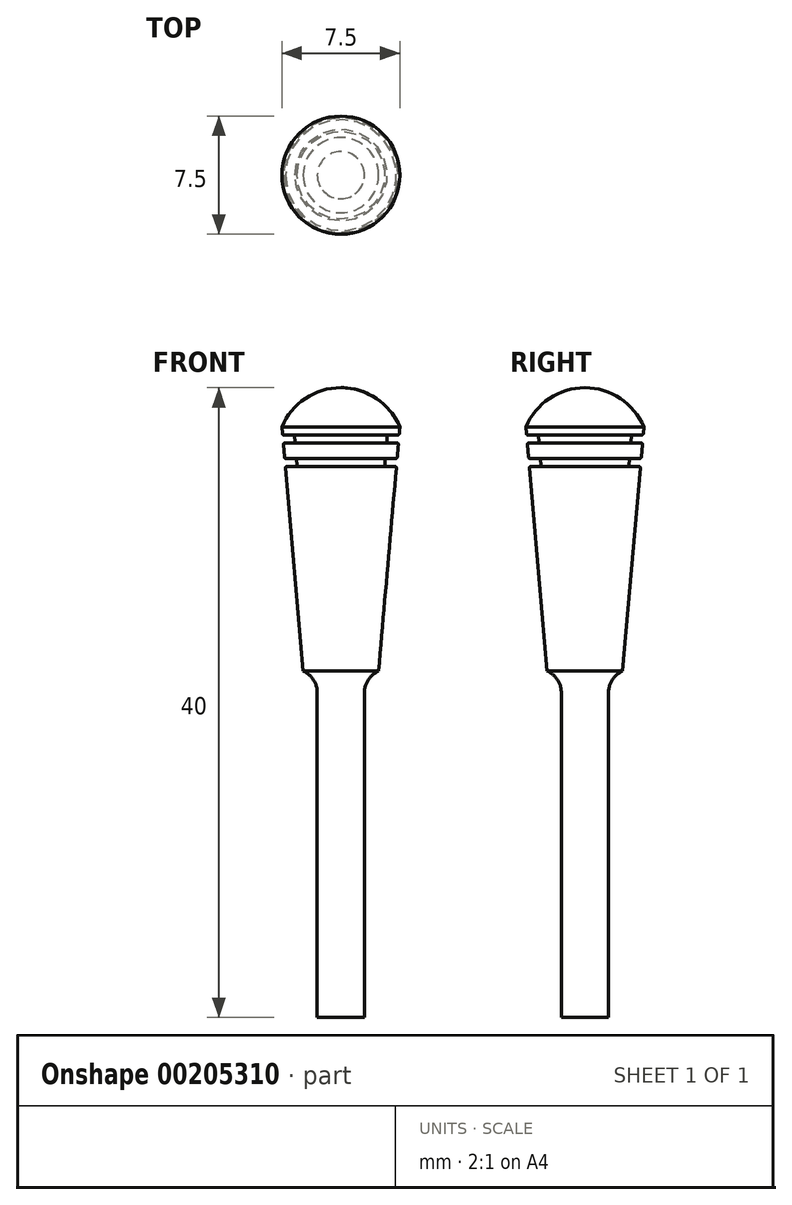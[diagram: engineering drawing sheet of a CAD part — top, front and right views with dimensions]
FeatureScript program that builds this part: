
annotation { "Feature Type Name" : "Feature", "Feature Type Description" : "" }
export const myFeature = defineFeature(function(context is Context, id is Id, definition is map)
    precondition{}
    {
        {
            var Q0;
            Q0=qCreatedBy(makeId("Front.planeOp"),FACE);
            var sketch = newSketch(context, id + "F0", { "sketchPlane" : qUnion([Q0])});
            skLineSegment(sketch, "E0.bottom", {"start": v(0, 0) * mm, "end": v(1.5, 0) * mm});
            skLineSegment(sketch, "E0.left", {"start": v(0, 0) * mm, "end": v(0, 21.67) * mm});
            skLineSegment(sketch, "E0.right", {"start": v(1.5, 0) * mm, "end": v(1.5, 22) * mm});
            skLineSegment(sketch, "E1", {"start": v(1.5, 22) * mm, "end": v(2.4, 22) * mm});
            skLineSegment(sketch, "E2", {"start": v(2.4, 22) * mm, "end": v(3.53, 35) * mm});
            skLineSegment(sketch, "E3", {"start": v(0, 21.67) * mm, "end": v(0, 37.5) * mm});
            skLineSegment(sketch, "E4", {"start": v(0, 37.5) * mm, "end": v(3.75, 37.5) * mm, "construction": true});
            skArc(sketch, "E5", {"start": v(3.75, 37.5) * mm, "mid": v(2.25, 39.32) * mm, "end": v(0, 40) * mm});
            skLineSegment(sketch, "E6", {"start": v(0, 40) * mm, "end": v(0, 37.5) * mm});
            skLineSegment(sketch, "E7", {"start": v(3.58, 35.5) * mm, "end": v(2.83, 35.5) * mm});
            skLineSegment(sketch, "E8", {"start": v(2.83, 35.5) * mm, "end": v(2.78, 35) * mm});
            skLineSegment(sketch, "E9", {"start": v(2.78, 35) * mm, "end": v(3.53, 35) * mm});
            skLineSegment(sketch, "E10.trimOffspring", {"start": v(3.58, 35.5) * mm, "end": v(3.66, 36.5) * mm});
            skLineSegment(sketch, "E11.1.0.0", {"start": v(3.7, 37) * mm, "end": v(2.96, 37) * mm});
            skLineSegment(sketch, "E11.1.0.1", {"start": v(2.96, 37) * mm, "end": v(2.91, 36.5) * mm});
            skLineSegment(sketch, "E11.1.0.2", {"start": v(2.91, 36.5) * mm, "end": v(3.66, 36.5) * mm});
            skLineSegment(sketch, "E11.direction1", {"start": v(2.83, 35.5) * mm, "end": v(2.96, 37) * mm, "construction": true});
            skLineSegment(sketch, "E12.trimOffspring", {"start": v(3.7, 37) * mm, "end": v(3.75, 37.5) * mm});
            skSolve(sketch);
        }
        {
            var Q0;
            Q0=makeQuery(id+"F0.imprint","IMPRINT",FACE,{"disambiguationData":[TD([[makeQuery(id+"F0.imprint","IMPRINT",EDGE,{"derivedFrom":sQuery(id+"F0.wireOp",EDGE,"E0.bottom")}),1.0]])]});
            var Q1;
            Q1=sQuery(id+"F0.wireOp",EDGE,"E3");
            revolve(context, id + "F1", {"entities" : qUnion([Q0]), "axis" : qUnion([Q1]), "revolveType" : RevolveType.FULL});
        }
        {
            var Q0;
            Q0=makeQuery(id+"F1.opRevolve","SWEPT_EDGE",EDGE,{"disambiguationData":[OSD([sQuery(id+"F0.wireOp",EDGE,"E0.right"),sQuery(id+"F0.wireOp",EDGE,"E1")])]});
            fillet(context, id + "F2", {"entities" : qUnion([Q0]), "radius" : 1.5 * mm, "tangentPropagation" : true, "allowEdgeOverflow" : false});
        }
        {
            var Q0;
            Q0=makeQuery(id+"F1.opRevolve","SWEPT_EDGE",EDGE,{"disambiguationData":[OSD([sQuery(id+"F0.wireOp",EDGE,"E7"),sQuery(id+"F0.wireOp",EDGE,"E8")])]});
            var Q1;
            Q1=makeQuery(id+"F1.opRevolve","SWEPT_EDGE",EDGE,{"disambiguationData":[OSD([sQuery(id+"F0.wireOp",EDGE,"E8"),sQuery(id+"F0.wireOp",EDGE,"E9")])]});
            var Q2;
            Q2=makeQuery(id+"F1.opRevolve","SWEPT_EDGE",EDGE,{"disambiguationData":[OSD([sQuery(id+"F0.wireOp",EDGE,"E2"),sQuery(id+"F0.wireOp",EDGE,"E9")])]});
            var Q3;
            Q3=makeQuery(id+"F1.opRevolve","SWEPT_EDGE",EDGE,{"disambiguationData":[OSD([sQuery(id+"F0.wireOp",EDGE,"E7"),sQuery(id+"F0.wireOp",EDGE,"E10.trimOffspring")])]});
            var Q4;
            Q4=makeQuery(id+"F1.opRevolve","SWEPT_FACE",FACE,{"disambiguationData":[OSD([sQuery(id+"F0.wireOp",EDGE,"E11.1.0.1")])]});
            var Q5;
            Q5=makeQuery(id+"F1.opRevolve","SWEPT_EDGE",EDGE,{"disambiguationData":[OSD([sQuery(id+"F0.wireOp",EDGE,"E10.trimOffspring"),sQuery(id+"F0.wireOp",EDGE,"E11.1.0.2")])]});
            var Q6;
            Q6=makeQuery(id+"F1.opRevolve","SWEPT_EDGE",EDGE,{"disambiguationData":[OSD([sQuery(id+"F0.wireOp",EDGE,"E11.1.0.0"),sQuery(id+"F0.wireOp",EDGE,"E12.trimOffspring")])]});
            fillet(context, id + "F3", {"entities" : qUnion([Q0, Q1, Q2, Q3, Q4, Q5, Q6]), "radius" : 0.1 * mm, "tangentPropagation" : true, "allowEdgeOverflow" : false});
        }
    });
